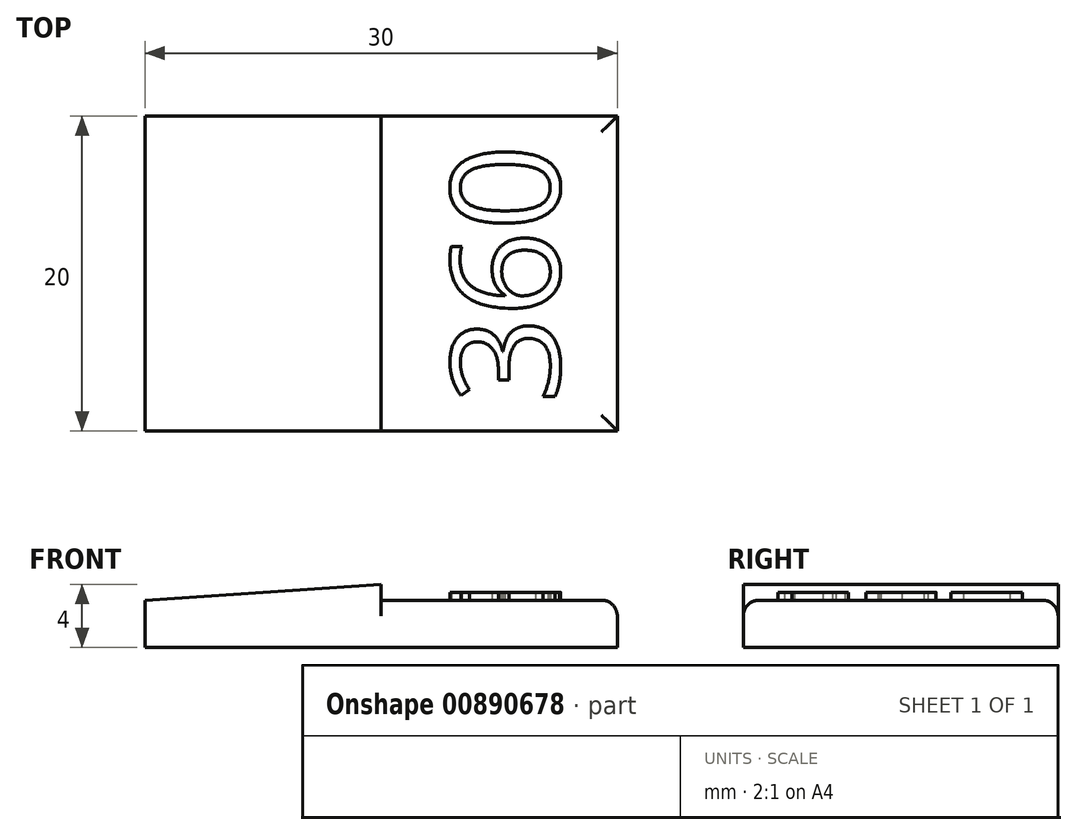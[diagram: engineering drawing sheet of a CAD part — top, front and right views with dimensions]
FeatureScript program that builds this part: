
annotation { "Feature Type Name" : "Feature", "Feature Type Description" : "" }
export const myFeature = defineFeature(function(context is Context, id is Id, definition is map)
    precondition{}
    {
        {
            var Q0;
            Q0=qCreatedBy(makeId("Front.planeOp"),FACE);
            var sketch = newSketch(context, id + "F0", { "sketchPlane" : qUnion([Q0])});
            skLineSegment(sketch, "E0.bottom", {"start": v(0, 0) * mm, "end": v(30, 0) * mm});
            skLineSegment(sketch, "E0.left", {"start": v(0, 0) * mm, "end": v(0, 3) * mm});
            skLineSegment(sketch, "E0.right", {"start": v(30, 0) * mm, "end": v(30, 3) * mm});
            skLineSegment(sketch, "E1", {"start": v(15, 4) * mm, "end": v(15, 3) * mm});
            skLineSegment(sketch, "E2", {"start": v(15, 3) * mm, "end": v(30, 3) * mm});
            skLineSegment(sketch, "E3", {"start": v(15, 4) * mm, "end": v(0, 3) * mm});
            skPoint(sketch, "E4.orphan", {"position": v(0, 4) * mm});
            skPoint(sketch, "E5.orphan", {"position": v(30, 4) * mm});
            skSolve(sketch);
        }
        {
            var Q0;
            Q0=makeQuery(id+"F0.imprint","IMPRINT",FACE,{"disambiguationData":[TD([[makeQuery(id+"F0.imprint","IMPRINT",EDGE,{"derivedFrom":sQuery(id+"F0.wireOp",EDGE,"E0.bottom")}),1.0]])]});
            extrude(context, id + "F1", {"entities" : qUnion([Q0]), "depth" : 20 * mm, "offsetDistance" : 25 * mm});
        }
        {
            var Q0;
            Q0=makeQuery(id+"F1.opExtrude","SWEPT_FACE",FACE,{"disambiguationData":[OSD([sQuery(id+"F0.wireOp",EDGE,"E2")])]});
            var sketch = newSketch(context, id + "F2", { "sketchPlane" : qUnion([Q0])});
            skText(sketch, "E6", { "text": "360", "fontName": "OpenSans-Regular.ttf"});
            const initialGuessF2  = {"E6": [0.02631, -0.01824, 0, 1, 0.0069]};
            skSetInitialGuess(sketch, initialGuessF2);
            skSolve(sketch);
        }
        {
            var Q0;
            Q0 = qSketchRegion(id + "F2", true);
            extrude(context, id + "F3", {"entities" : qUnion([Q0]), "operationType" : NewBodyOperationType.ADD, "depth" : 0.5 * mm, "offsetDistance" : 25 * mm});
        }
        {
            var Q0;
            Q0=makeQuery(id+"F1.opExtrude","CAP_EDGE",EDGE,{"disambiguationData":[OSD([sQuery(id+"F0.wireOp",EDGE,"E2")])],"isStart":false});
            var Q1;
            Q1=makeQuery(id+"F1.opExtrude","SWEPT_EDGE",EDGE,{"disambiguationData":[OSD([sQuery(id+"F0.wireOp",EDGE,"E0.right"),sQuery(id+"F0.wireOp",EDGE,"E2")])]});
            var Q2;
            Q2=makeQuery(id+"F1.opExtrude","CAP_EDGE",EDGE,{"disambiguationData":[OSD([sQuery(id+"F0.wireOp",EDGE,"E2")])],"isStart":true});
            fillet(context, id + "F4", {"entities" : qUnion([Q0, Q1, Q2]), "radius" : 1 * mm, "tangentPropagation" : true, "allowEdgeOverflow" : false});
        }
    });
